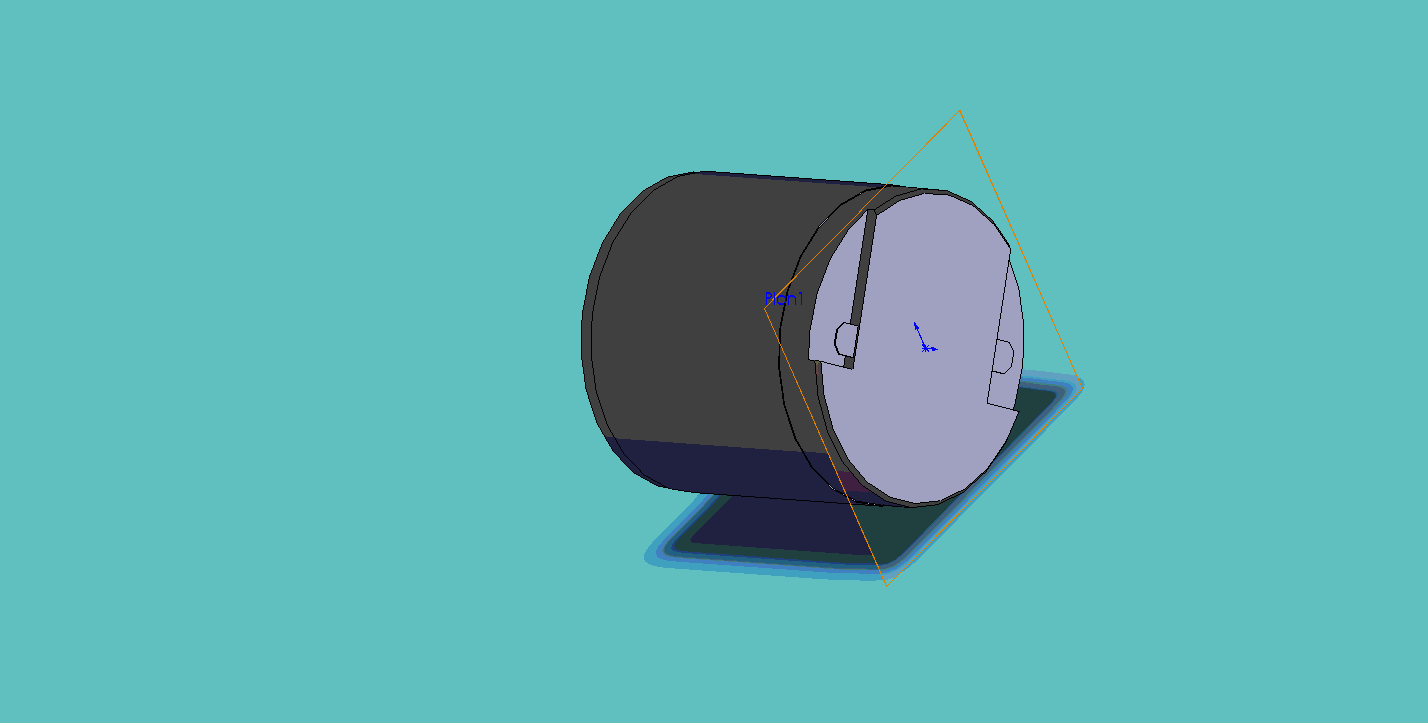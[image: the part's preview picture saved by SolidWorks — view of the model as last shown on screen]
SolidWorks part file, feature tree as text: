
SOLIDWORKS PART (.sldprt)
format: sldprt  version: not decoded by parser v0  size: 204,800 bytes
history: native  units: mm
features: plane x4, chamfer x4, sketch x3, material x1, revolve x1, cut_extrude x1, extrude x1 (+8 scaffold rows collapsed)
feature tree (23):
  scaffold x8  (default folders/planes/origin — collapsed)
  material  "Matériau <non spécifié>"
  plane  "Plan de face"
  plane  "Plan de dessus"
  plane  "Plan de droite"
  sketch  "Esquisse1"  dims[D1=30.0mm D2=29.8mm D3=29.7mm D4=30.0mm D5=4.9mm D6=1.4mm D7=8.0mm D8=2.0mm D9=8.2mm D10=4.2mm D11=2.0mm D12=1.1mm]
  revolve  "Révolution1"  Angle=360deg
  sketch  "Esquisse2"  dims[c1.D1=~20.492854mm c2.D1=45.0deg c2.D2=19.0mm c2.D3=3.6mm]
  cut_extrude  "Enlèv. mat.-Extru.2"  Depth=1.2mm
  chamfer  "Chanfrein1"  Distance=0.2mm Angle=45deg
  plane  "Plan1"  Offset=0.3mm
  sketch  "Esquisse3"  dims[D1=3.0mm D2=2.75mm D3=0.5mm D4=0.5mm]
  extrude  "Extrusion1"  Depth=0.13mm
  chamfer  "Chanfrein2"  Distance=0.8mm Angle=45deg
  chamfer  "Chanfrein3"  Distance=0.4mm Angle=45deg
  chamfer  "Chanfrein4"  Distance=0.2mm Angle=30deg
decode coverage: 10 of 10 modeling features carry decoded parameters
note: ~ marks probable driven/reference dimensions
note: suppression state not decoded; provenance and decode notes live in map.json
